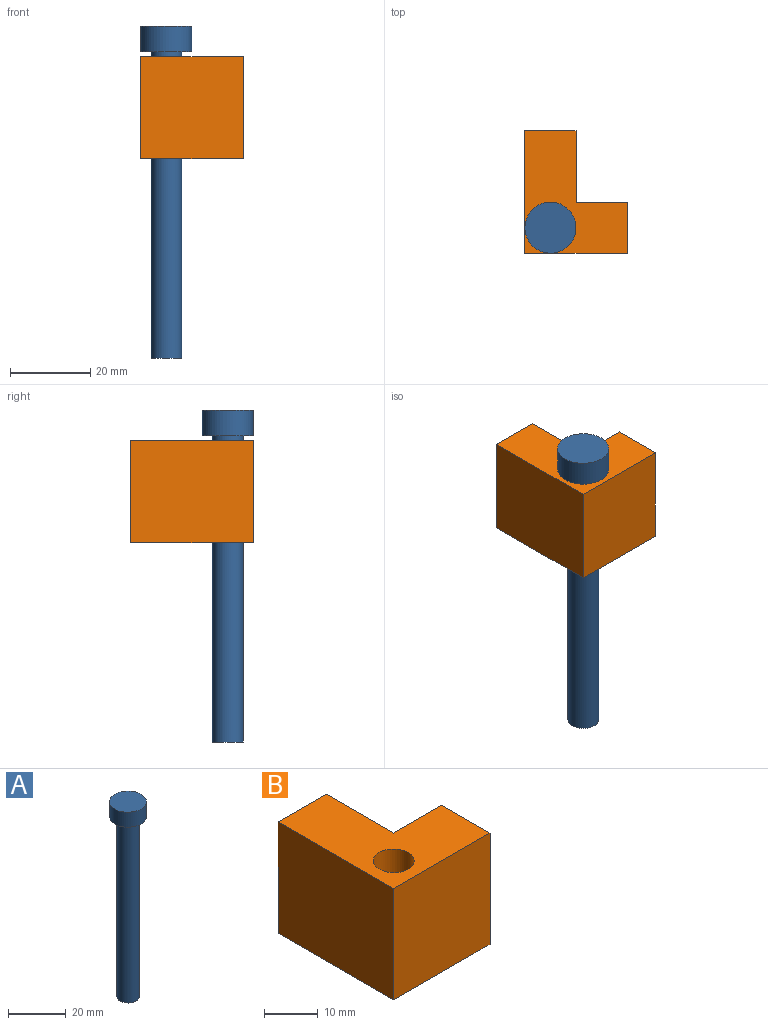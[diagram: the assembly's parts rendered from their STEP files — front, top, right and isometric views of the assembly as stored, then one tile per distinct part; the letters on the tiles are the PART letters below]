
ASSEMBLY  parts=2 mates=1
PART A: 5 faces, bbox 12.7x12.7x82.6 mm
  f0: cylinder r=3.81mm len=76.2mm, axis (0,0,-1), area 1824.1mm2, adj f1,f4
  f1: plane 7.62x7.62mm, normal (0,0,-1), area 45.6mm2, adj f0
  f2: cylinder r=6.35mm len=12.7mm, axis (0,0,-1), area 253.4mm2, adj f3,f4
  f3: plane 12.7x12.7mm, normal (0,0,1), area 126.7mm2, adj f2
  f4: plane 12.7x12.7mm, normal (0,0,-1), area 81.1mm2, adj f0,f2
PART B: 9 faces, bbox 25.4x30.5x25.4 mm
  f0: plane 25.4x12.7mm, normal (0,1,0), area 322.6mm2, adj f1,f5,f6,f7
  f1: plane 30.48x25.4mm, normal (-1,0,0), area 774.2mm2, adj f0,f2,f6,f7
  f2: plane 25.4x25.4mm, normal (0,-1,0), area 645.2mm2, adj f1,f3,f6,f7
  f3: plane 25.4x12.7mm, normal (1,0,0), area 322.6mm2, adj f2,f4,f6,f7
  f4: plane 25.4x12.7mm, normal (0,1,0), area 322.6mm2, adj f3,f5,f6,f7
  f5: plane 25.4x17.78mm, normal (1,0,0), area 451.6mm2, adj f0,f4,f6,f7
  f6: plane 30.48x25.4mm, normal (0,0,1), area 502.8mm2, adj f0,f1,f2,f3,f4,f5,f8
  f7: plane 30.48x25.4mm, normal (0,0,-1), area 502.8mm2, adj f0,f1,f2,f3,f4,f5,f8
  f8: cylinder r=3.81mm len=25.4mm, axis (0,0,1), area 608mm2, adj f6,f7
PLACE A rot(axis=(0,0,-1),76.8deg) t=(-19.17,-45.19,-61.01)mm
PLACE B t=(-10.69,0.86,-11.5)mm fixed
MATE cylindrical A.f0 <-> B.f8  axis (0,0,-1) through (-4.34,7.21,-61.01)mm
